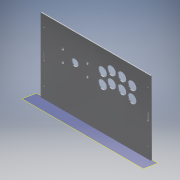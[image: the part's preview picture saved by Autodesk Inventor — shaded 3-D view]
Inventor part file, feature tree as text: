
AUTODESK INVENTOR PART (.ipt)
format: ipt  version: 2019 (Build 230136000, 136)  size: 218,112 bytes
history: native  units: in
note: dims shown in document units (in); Inventor stores cm internally (conversion verified against a paired STEP export)
features: other x11, reference x8, hole x4, extrude x2, fillet x2
ambient origin geometry x8: Origin, YZ Plane, XZ Plane, XY Plane, X Axis, Y Axis, Z Axis, Center Point
bodies: Body1 (feature_tree)
feature tree (27):
  other  "TopPanel"
  other  "Panel"
  other  "JoystickMount"
  other  "ButtonMounts"
  extrude  "PanelExtrusion"  Depth=10.0in
  hole  "JoystickScrews"  [1 undecoded]
  hole  "JoystickShaft"  [1 undecoded]
  hole  "ButtonHoles"  [1 undecoded]
  fillet  "Corners"  Radius=1.5354in
  other  "10DegOffsetAlignment"
  hole  "PanelBoltHoles"  [1 undecoded]
  extrude  "TabSlotExtrusion"  Depth=1.5354in
  fillet  "TabSlotFillets"  Radius=1.5354in
  other  "ScrewHoleCenters"
  reference  "Reference1"
  reference  "Reference2"
  reference  "Reference3"
  reference  "Reference4"
  reference  "Reference5"
  reference  "Reference6"
  reference  "Reference7"
  reference  "Reference8"
  other  "TabSlotSketch"
  parser-record x1  (decoder bookkeeping rows leaked as tree rows — omitted from the tree; the rows remain in map.json)
  other  "ArcadeController.iam"
  other  "Panel_side:1"
  other  "Panel_side:2"
note: 4 required parameter values undecoded (feature->parameter linkage not recoverable at this tier; creation-order binding heuristic only, values carry confidence <= 0.55)
note: 1 file-system path scrubbed to <path> (originals preserved in map.json)
